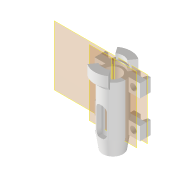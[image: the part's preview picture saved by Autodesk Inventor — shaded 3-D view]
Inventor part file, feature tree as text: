
AUTODESK INVENTOR PART (.ipt)
format: ipt  version: 2022 (Build 260153000, 153)  size: 379,904 bytes
history: native  units: mm
features: sketch x8, extrude x6, other x6, projected_geometry x4, plane x3, revolve x2, mirror x2, reference x1
ambient origin geometry x8: Origin, YZ Plane, XZ Plane, XY Plane, X Axis, Y Axis, Z Axis, Center Point
bodies: Volumenkörper1 (feature_tree)
feature tree (32):
  plane  "Arbeitsebene1"
  extrude  "Extrusion1"  Depth=3.0mm
  extrude  "Extrusion2"  Depth=34.0mm
  extrude  "Extrusion3"  Depth=6.0mm
  extrude  "Extrusion4"  Depth=6.0mm
  extrude  "Extrusion5"  Depth=6.0mm
  other  "Arbeitsachse1"
  revolve  "Umdrehung1"
  plane  "Arbeitsebene2"
  mirror  "Spiegeln2"
  revolve  "Umdrehung2"
  mirror  "Spiegeln3"
  extrude  "Extrusion6"  Depth=6.1mm
  sketch  "Skizze1"  dims[d0=6.0mm d1=3.0mm]
  sketch  "Skizze2"  dims[d2=6.0mm d3=34.0mm]
  reference  "Referenz1"
  sketch  "Skizze3"  dims[d4=8.0mm d5=6.0mm]
  projected_geometry  "Projizierte Kontur1"
  sketch  "Skizze4"  dims[d6=6.0mm d7=6.0mm]
  projected_geometry  "Projizierte Kontur2"
  sketch  "Skizze5"  dims[d8=6.0mm d9=6.0mm]
  sketch  "Skizze6"  dims[d10=6.0mm d11=6.1mm]
  projected_geometry  "Projizierte Kontur3"
  other  "Arbeitspunkt1"
  sketch  "Skizze7"  dims[d12=6.1mm]
  other  "Arbeitsachse2"
  plane  "Arbeitsebene3"
  sketch  "Skizze8"  dims[d13=6.0mm d14=6.0mm d15=0.0mm d16=4.0mm d17=90.0deg d18=15.0deg d19=15.0deg d20=6.0mm d21=0.0mm d22=6.0mm d23=3.93mm d24=0.0mm d25=12.0mm d26=0.0mm d27=14.65mm d28=10.0mm d29=4.0mm d30=10.0mm d31=0.0mm d32=0.0mm d33=0.0mm d36=9.5mm d37=9.5mm d38=3.0mm d39=45.0deg d40=3.0mm d41=11.25mm d42=16.75mm d43=3.0mm d44=6.108652mm d45=14.0mm d47=5.25mm d48=180.0deg d49=0.0mm d50=0.0mm]
  projected_geometry  "Projizierte Kontur4"
  other  "<userpath>\Documents\GitHub\VolterVOneHACKS\INVENTOR\VolteraOne_tool.ipj.iam"
  other  "VolteraOne_tool.ipj.iam"
  other  "00_rod_6mm:1"
